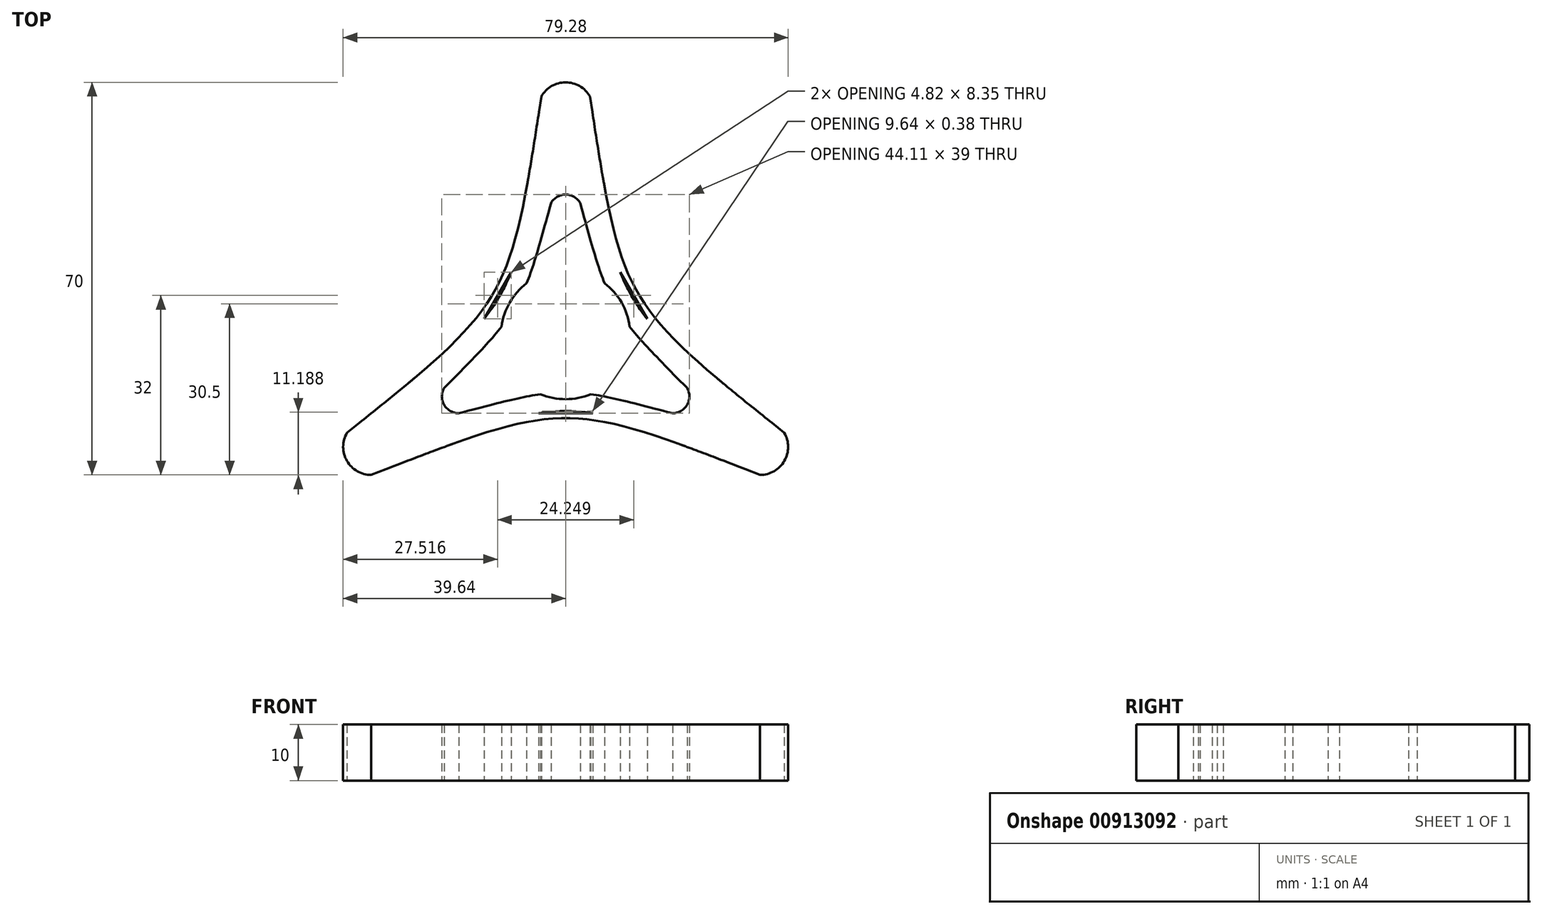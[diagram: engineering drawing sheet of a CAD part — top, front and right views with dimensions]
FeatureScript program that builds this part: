
annotation { "Feature Type Name" : "Feature", "Feature Type Description" : "" }
export const myFeature = defineFeature(function(context is Context, id is Id, definition is map)
    precondition{}
    {
        {
            var Q0;
            Q0=qCreatedBy(makeId("Top.planeOp"),FACE);
            var sketch = newSketch(context, id + "F0", { "sketchPlane" : qUnion([Q0])});
            skCircle(sketch, "E0", {"center": v(0, 0) * mm, "radius": 11.5 * mm});
            skCircle(sketch, "E1", {"center": v(0, 0) * mm, "radius": 40 * mm});
            skCircle(sketch, "E2", {"center": v(0, 0) * mm, "radius": 28 * mm});
            skCircle(sketch, "E3", {"center": v(0, 0) * mm, "radius": 9 * mm});
            skCircle(sketch, "E4.cCircle", {"center": v(0, 0) * mm, "radius": 9 * mm, "construction": true});
            skLineSegment(sketch, "E4.0", {"start": v(0, -9) * mm, "end": v(-7.8, 4.5) * mm});
            skLineSegment(sketch, "E4.1", {"start": v(-7.8, 4.5) * mm, "end": v(7.8, 4.5) * mm});
            skLineSegment(sketch, "E4.2", {"start": v(7.8, 4.5) * mm, "end": v(0, -9) * mm});
            skCircle(sketch, "E5.cCircle", {"center": v(0, 0) * mm, "radius": 11.5 * mm, "construction": true});
            skLineSegment(sketch, "E5.0", {"start": v(0, -11.5) * mm, "end": v(-9.96, 5.75) * mm});
            skLineSegment(sketch, "E5.1", {"start": v(-9.96, 5.75) * mm, "end": v(9.96, 5.75) * mm});
            skLineSegment(sketch, "E5.2", {"start": v(9.96, 5.75) * mm, "end": v(0, -11.5) * mm});
            skCircle(sketch, "E6.cCircle", {"center": v(0, 0) * mm, "radius": 28 * mm, "construction": true});
            skLineSegment(sketch, "E6.0", {"start": v(2.6, 23.5) * mm, "end": v(21.65, -9.5) * mm});
            skLineSegment(sketch, "E6.1", {"start": v(19.05, -14) * mm, "end": v(-19.05, -14) * mm});
            skLineSegment(sketch, "E6.2", {"start": v(-21.65, -9.5) * mm, "end": v(-2.6, 23.5) * mm});
            skCircle(sketch, "E7.cCircle", {"center": v(0, 0) * mm, "radius": 40 * mm, "construction": true});
            skPoint(sketch, "E7.cCircle.perimeterSnap0", {"position": v(0, 4.5) * mm});
            skLineSegment(sketch, "E7.0", {"start": v(4.33, 32.5) * mm, "end": v(30.31, -12.5) * mm});
            skPoint(sketch, "E7.0.startSnap0", {"position": v(0, 4.5) * mm});
            skLineSegment(sketch, "E7.1", {"start": v(25.98, -20) * mm, "end": v(-25.98, -20) * mm});
            skLineSegment(sketch, "E7.2", {"start": v(-30.31, -12.5) * mm, "end": v(-4.33, 32.5) * mm});
            skPoint(sketch, "E8.visualSharp", {"position": v(0, 40) * mm});
            skArc(sketch, "E8.filletArc", {"start": v(4.33, 32.5) * mm, "mid": v(0, 35) * mm, "end": v(-4.33, 32.5) * mm});
            skPoint(sketch, "E9.visualSharp", {"position": v(0, 28) * mm});
            skArc(sketch, "E9.filletArc", {"start": v(2.6, 23.5) * mm, "mid": v(0, 25) * mm, "end": v(-2.6, 23.5) * mm});
            skPoint(sketch, "E10.visualSharp", {"position": v(34.64, -20) * mm});
            skArc(sketch, "E10.filletArc", {"start": v(25.98, -20) * mm, "mid": v(30.31, -17.5) * mm, "end": v(30.31, -12.5) * mm});
            skPoint(sketch, "E11.visualSharp", {"position": v(24.25, -14) * mm});
            skArc(sketch, "E11.filletArc", {"start": v(19.05, -14) * mm, "mid": v(21.65, -12.5) * mm, "end": v(21.65, -9.5) * mm});
            skPoint(sketch, "E12.visualSharp", {"position": v(-24.25, -14) * mm});
            skArc(sketch, "E12.filletArc", {"start": v(-21.65, -9.5) * mm, "mid": v(-21.65, -12.5) * mm, "end": v(-19.05, -14) * mm});
            skPoint(sketch, "E13.visualSharp", {"position": v(-34.64, -20) * mm});
            skArc(sketch, "E13.filletArc", {"start": v(-30.31, -12.5) * mm, "mid": v(-30.31, -17.5) * mm, "end": v(-25.98, -20) * mm});
            skFitSpline(sketch, "E14", {"points": [v(4.33, 32.5) * mm, v(30.31, -12.5) * mm], "startDerivative": vector(16.89, -80.25) * mm, "endDerivative": vector(61.05, -54.75) * mm});
            skFitSpline(sketch, "E15", {"points": [v(2.6, 23.5) * mm, v(21.65, -9.5) * mm], "startDerivative": vector(15.59, -57) * mm, "endDerivative": vector(41.57, -42) * mm});
            skFitSpline(sketch, "E16", {"points": [v(-2.6, 23.5) * mm, v(-21.65, -9.5) * mm], "startDerivative": vector(-15.59, -57) * mm, "endDerivative": vector(-41.57, -42) * mm});
            skFitSpline(sketch, "E17", {"points": [v(-4.33, 32.5) * mm, v(-30.31, -12.5) * mm], "startDerivative": vector(-16.89, -80.25) * mm, "endDerivative": vector(-61.05, -54.75) * mm});
            skFitSpline(sketch, "E18", {"points": [v(-19.05, -14) * mm, v(19.05, -14) * mm], "startDerivative": vector(57.16, 15) * mm, "endDerivative": vector(57.16, -15) * mm});
            skFitSpline(sketch, "E19", {"points": [v(-25.98, -20) * mm, v(25.98, -20) * mm], "startDerivative": vector(77.94, 25.5) * mm, "endDerivative": vector(77.94, -25.5) * mm});
            skCircle(sketch, "E20", {"center": v(0, 0) * mm, "radius": 50 * mm});
            skCircle(sketch, "E21.cCircle", {"center": v(0, 0) * mm, "radius": 50 * mm, "construction": true});
            skLineSegment(sketch, "E21.0", {"start": v(4.33, 42.5) * mm, "end": v(38.97, -17.5) * mm});
            skLineSegment(sketch, "E21.1", {"start": v(34.64, -25) * mm, "end": v(-34.64, -25) * mm});
            skLineSegment(sketch, "E21.2", {"start": v(-38.97, -17.5) * mm, "end": v(-4.33, 42.5) * mm});
            skPoint(sketch, "E22.visualSharp", {"position": v(0, 50) * mm});
            skArc(sketch, "E22.filletArc", {"start": v(4.33, 42.5) * mm, "mid": v(0, 45) * mm, "end": v(-4.33, 42.5) * mm});
            skPoint(sketch, "E23.visualSharp", {"position": v(-43.3, -25) * mm});
            skArc(sketch, "E23.filletArc", {"start": v(-38.97, -17.5) * mm, "mid": v(-38.97, -22.5) * mm, "end": v(-34.64, -25) * mm});
            skPoint(sketch, "E24.visualSharp", {"position": v(43.3, -25) * mm});
            skArc(sketch, "E24.filletArc", {"start": v(34.64, -25) * mm, "mid": v(38.97, -22.5) * mm, "end": v(38.97, -17.5) * mm});
            skFitSpline(sketch, "E25", {"points": [v(4.33, 42.5) * mm, v(38.97, -17.5) * mm], "startDerivative": vector(16.89, -110.25) * mm, "endDerivative": vector(87.04, -69.75) * mm});
            skFitSpline(sketch, "E26", {"points": [v(-4.33, 42.5) * mm, v(-38.97, -17.5) * mm], "startDerivative": vector(-16.89, -110.25) * mm, "endDerivative": vector(-87.04, -69.75) * mm});
            skFitSpline(sketch, "E27", {"points": [v(-34.64, -25) * mm, v(34.64, -25) * mm], "startDerivative": vector(103.92, 40.5) * mm, "endDerivative": vector(103.92, -40.5) * mm});
            skSolve(sketch);
        }
        {
            var Q0;
            {var subQ5=sQuery(id+"F0.wireOp",EDGE,"E8.filletArc");Q0=makeQuery(id+"F0.imprint","IMPRINT",FACE,{"disambiguationData":[TD([[makeQuery(id+"F0.imprint","IMPRINT",EDGE,{"derivedFrom":subQ5}),1.0]])]});}
            var Q1;
            {var subQ0=sQuery(id+"F0.wireOp",EDGE,"E9.filletArc");Q1=makeQuery(id+"F0.imprint","IMPRINT",FACE,{"disambiguationData":[TD([[makeQuery(id+"F0.imprint","IMPRINT",EDGE,{"derivedFrom":subQ0}),-1.0]])]});}
            var Q2;
            {var subQ1=sQuery(id+"F0.wireOp",EDGE,"E6.0");var subQ3=sQuery(id+"F0.wireOp",EDGE,"E14");var subQ4=makeQuery(id+"F0.imprint","INTERSECT",VERTEX,{"disambiguationData":[OD(0.0)],"derivedFrom":[subQ1,subQ3]});Q2=makeQuery(id+"F0.imprint","IMPRINT",FACE,{"disambiguationData":[TD([[makeQuery(id+"F0.imprint","IMPRINT",EDGE,{"disambiguationData":[TD([[subQ4,-1.0]])],"derivedFrom":subQ3}),-1.0]])]});}
            var Q3;
            {var subQ5=sQuery(id+"F0.wireOp",EDGE,"E10.filletArc");Q3=makeQuery(id+"F0.imprint","IMPRINT",FACE,{"disambiguationData":[TD([[makeQuery(id+"F0.imprint","IMPRINT",EDGE,{"derivedFrom":subQ5}),1.0]])]});}
            var Q4;
            {var subQ0=sQuery(id+"F0.wireOp",EDGE,"E11.filletArc");Q4=makeQuery(id+"F0.imprint","IMPRINT",FACE,{"disambiguationData":[TD([[makeQuery(id+"F0.imprint","IMPRINT",EDGE,{"derivedFrom":subQ0}),-1.0]])]});}
            var Q5;
            {var subQ1=sQuery(id+"F0.wireOp",EDGE,"E6.1");var subQ3=sQuery(id+"F0.wireOp",EDGE,"E19");var subQ6=makeQuery(id+"F0.imprint","INTERSECT",VERTEX,{"disambiguationData":[OD(0.0)],"derivedFrom":[subQ1,subQ3]});Q5=makeQuery(id+"F0.imprint","IMPRINT",FACE,{"disambiguationData":[TD([[makeQuery(id+"F0.imprint","IMPRINT",EDGE,{"disambiguationData":[TD([[subQ6,1.0]])],"derivedFrom":subQ3}),1.0]])]});}
            var Q6;
            {var subQ0=sQuery(id+"F0.wireOp",EDGE,"E12.filletArc");Q6=makeQuery(id+"F0.imprint","IMPRINT",FACE,{"disambiguationData":[TD([[makeQuery(id+"F0.imprint","IMPRINT",EDGE,{"derivedFrom":subQ0}),-1.0]])]});}
            var Q7;
            {var subQ5=sQuery(id+"F0.wireOp",EDGE,"E13.filletArc");Q7=makeQuery(id+"F0.imprint","IMPRINT",FACE,{"disambiguationData":[TD([[makeQuery(id+"F0.imprint","IMPRINT",EDGE,{"derivedFrom":subQ5}),1.0]])]});}
            var Q8;
            {var subQ1=sQuery(id+"F0.wireOp",EDGE,"E6.2");var subQ3=sQuery(id+"F0.wireOp",EDGE,"E17");var subQ5=makeQuery(id+"F0.imprint","INTERSECT",VERTEX,{"disambiguationData":[OD(0.0)],"derivedFrom":[subQ1,subQ3]});Q8=makeQuery(id+"F0.imprint","IMPRINT",FACE,{"disambiguationData":[TD([[makeQuery(id+"F0.imprint","IMPRINT",EDGE,{"disambiguationData":[TD([[subQ5,1.0]])],"derivedFrom":subQ3}),1.0]])]});}
            extrude(context, id + "F1", {"entities" : qUnion([Q0, Q1, Q2, Q3, Q4, Q5, Q6, Q7, Q8]), "depth" : 10 * mm, "offsetDistance" : 25 * mm});
        }
        {
            var Q0;
            {var subQ5=sQuery(id+"F0.wireOp",EDGE,"E8.filletArc");Q0=makeQuery(id+"F0.imprint","IMPRINT",FACE,{"disambiguationData":[TD([[makeQuery(id+"F0.imprint","IMPRINT",EDGE,{"derivedFrom":subQ5}),1.0]])]});}
            var Q1;
            {var subQ0=sQuery(id+"F0.wireOp",EDGE,"E9.filletArc");Q1=makeQuery(id+"F0.imprint","IMPRINT",FACE,{"disambiguationData":[TD([[makeQuery(id+"F0.imprint","IMPRINT",EDGE,{"derivedFrom":subQ0}),-1.0]])]});}
            var Q2;
            {var subQ1=sQuery(id+"F0.wireOp",EDGE,"E6.2");var subQ3=sQuery(id+"F0.wireOp",EDGE,"E17");var subQ5=makeQuery(id+"F0.imprint","INTERSECT",VERTEX,{"disambiguationData":[OD(0.0)],"derivedFrom":[subQ1,subQ3]});Q2=makeQuery(id+"F0.imprint","IMPRINT",FACE,{"disambiguationData":[TD([[makeQuery(id+"F0.imprint","IMPRINT",EDGE,{"disambiguationData":[TD([[subQ5,1.0]])],"derivedFrom":subQ3}),1.0]])]});}
            var Q3;
            {var subQ1=sQuery(id+"F0.wireOp",EDGE,"E6.0");var subQ3=sQuery(id+"F0.wireOp",EDGE,"E14");var subQ4=makeQuery(id+"F0.imprint","INTERSECT",VERTEX,{"disambiguationData":[OD(0.0)],"derivedFrom":[subQ1,subQ3]});Q3=makeQuery(id+"F0.imprint","IMPRINT",FACE,{"disambiguationData":[TD([[makeQuery(id+"F0.imprint","IMPRINT",EDGE,{"disambiguationData":[TD([[subQ4,-1.0]])],"derivedFrom":subQ3}),-1.0]])]});}
            var Q4;
            {var subQ0=sQuery(id+"F0.wireOp",EDGE,"E11.filletArc");Q4=makeQuery(id+"F0.imprint","IMPRINT",FACE,{"disambiguationData":[TD([[makeQuery(id+"F0.imprint","IMPRINT",EDGE,{"derivedFrom":subQ0}),-1.0]])]});}
            var Q5;
            {var subQ5=sQuery(id+"F0.wireOp",EDGE,"E10.filletArc");Q5=makeQuery(id+"F0.imprint","IMPRINT",FACE,{"disambiguationData":[TD([[makeQuery(id+"F0.imprint","IMPRINT",EDGE,{"derivedFrom":subQ5}),1.0]])]});}
            var Q6;
            {var subQ1=sQuery(id+"F0.wireOp",EDGE,"E6.1");var subQ3=sQuery(id+"F0.wireOp",EDGE,"E19");var subQ6=makeQuery(id+"F0.imprint","INTERSECT",VERTEX,{"disambiguationData":[OD(0.0)],"derivedFrom":[subQ1,subQ3]});Q6=makeQuery(id+"F0.imprint","IMPRINT",FACE,{"disambiguationData":[TD([[makeQuery(id+"F0.imprint","IMPRINT",EDGE,{"disambiguationData":[TD([[subQ6,1.0]])],"derivedFrom":subQ3}),1.0]])]});}
            var Q7;
            {var subQ0=sQuery(id+"F0.wireOp",EDGE,"E12.filletArc");Q7=makeQuery(id+"F0.imprint","IMPRINT",FACE,{"disambiguationData":[TD([[makeQuery(id+"F0.imprint","IMPRINT",EDGE,{"derivedFrom":subQ0}),-1.0]])]});}
            var Q8;
            {var subQ5=sQuery(id+"F0.wireOp",EDGE,"E13.filletArc");Q8=makeQuery(id+"F0.imprint","IMPRINT",FACE,{"disambiguationData":[TD([[makeQuery(id+"F0.imprint","IMPRINT",EDGE,{"derivedFrom":subQ5}),1.0]])]});}
            extrude(context, id + "F2", {"entities" : qUnion([Q0, Q1, Q2, Q3, Q4, Q5, Q6, Q7, Q8]), "operationType" : NewBodyOperationType.ADD, "depth" : 10 * mm, "offsetDistance" : 25 * mm});
        }
        {
            var Q0;
            {var subQ5=sQuery(id+"F0.wireOp",EDGE,"E10.filletArc");Q0=makeQuery(id+"F0.imprint","IMPRINT",FACE,{"disambiguationData":[TD([[makeQuery(id+"F0.imprint","IMPRINT",EDGE,{"derivedFrom":subQ5}),1.0]])]});}
            var Q1;
            {var subQ0=sQuery(id+"F0.wireOp",EDGE,"E11.filletArc");Q1=makeQuery(id+"F0.imprint","IMPRINT",FACE,{"disambiguationData":[TD([[makeQuery(id+"F0.imprint","IMPRINT",EDGE,{"derivedFrom":subQ0}),-1.0]])]});}
            var Q2;
            {var subQ5=sQuery(id+"F0.wireOp",EDGE,"E8.filletArc");Q2=makeQuery(id+"F0.imprint","IMPRINT",FACE,{"disambiguationData":[TD([[makeQuery(id+"F0.imprint","IMPRINT",EDGE,{"derivedFrom":subQ5}),1.0]])]});}
            var Q3;
            {var subQ5=sQuery(id+"F0.wireOp",EDGE,"E13.filletArc");Q3=makeQuery(id+"F0.imprint","IMPRINT",FACE,{"disambiguationData":[TD([[makeQuery(id+"F0.imprint","IMPRINT",EDGE,{"derivedFrom":subQ5}),1.0]])]});}
            var Q4;
            {var subQ0=sQuery(id+"F0.wireOp",EDGE,"E12.filletArc");Q4=makeQuery(id+"F0.imprint","IMPRINT",FACE,{"disambiguationData":[TD([[makeQuery(id+"F0.imprint","IMPRINT",EDGE,{"derivedFrom":subQ0}),-1.0]])]});}
            var Q5;
            {var subQ0=sQuery(id+"F0.wireOp",EDGE,"E9.filletArc");Q5=makeQuery(id+"F0.imprint","IMPRINT",FACE,{"disambiguationData":[TD([[makeQuery(id+"F0.imprint","IMPRINT",EDGE,{"derivedFrom":subQ0}),-1.0]])]});}
            var Q6;
            {var subQ1=sQuery(id+"F0.wireOp",EDGE,"E6.0");var subQ3=sQuery(id+"F0.wireOp",EDGE,"E14");var subQ4=makeQuery(id+"F0.imprint","INTERSECT",VERTEX,{"disambiguationData":[OD(0.0)],"derivedFrom":[subQ1,subQ3]});Q6=makeQuery(id+"F0.imprint","IMPRINT",FACE,{"disambiguationData":[TD([[makeQuery(id+"F0.imprint","IMPRINT",EDGE,{"disambiguationData":[TD([[subQ4,-1.0]])],"derivedFrom":subQ3}),-1.0]])]});}
            var Q7;
            {var subQ1=sQuery(id+"F0.wireOp",EDGE,"E6.2");var subQ3=sQuery(id+"F0.wireOp",EDGE,"E17");var subQ5=makeQuery(id+"F0.imprint","INTERSECT",VERTEX,{"disambiguationData":[OD(0.0)],"derivedFrom":[subQ1,subQ3]});Q7=makeQuery(id+"F0.imprint","IMPRINT",FACE,{"disambiguationData":[TD([[makeQuery(id+"F0.imprint","IMPRINT",EDGE,{"disambiguationData":[TD([[subQ5,1.0]])],"derivedFrom":subQ3}),1.0]])]});}
            var Q8;
            {var subQ1=sQuery(id+"F0.wireOp",EDGE,"E6.1");var subQ3=sQuery(id+"F0.wireOp",EDGE,"E19");var subQ6=makeQuery(id+"F0.imprint","INTERSECT",VERTEX,{"disambiguationData":[OD(0.0)],"derivedFrom":[subQ1,subQ3]});Q8=makeQuery(id+"F0.imprint","IMPRINT",FACE,{"disambiguationData":[TD([[makeQuery(id+"F0.imprint","IMPRINT",EDGE,{"disambiguationData":[TD([[subQ6,1.0]])],"derivedFrom":subQ3}),1.0]])]});}
            extrude(context, id + "F3", {"entities" : qUnion([Q0, Q1, Q2, Q3, Q4, Q5, Q6, Q7, Q8]), "operationType" : NewBodyOperationType.ADD, "depth" : 10 * mm, "offsetDistance" : 25 * mm});
        }
        {
            var Q0;
            {var subQ0=sQuery(id+"F0.wireOp",EDGE,"E8.filletArc");Q0=makeQuery(id+"F0.imprint","IMPRINT",FACE,{"disambiguationData":[TD([[makeQuery(id+"F0.imprint","IMPRINT",EDGE,{"derivedFrom":subQ0}),-1.0]])]});}
            var Q1;
            {var subQ5=sQuery(id+"F0.wireOp",EDGE,"E22.filletArc");Q1=makeQuery(id+"F0.imprint","IMPRINT",FACE,{"disambiguationData":[TD([[makeQuery(id+"F0.imprint","IMPRINT",EDGE,{"derivedFrom":subQ5}),1.0]])]});}
            var Q2;
            {var subQ0=sQuery(id+"F0.wireOp",EDGE,"E9.filletArc");Q2=makeQuery(id+"F0.imprint","IMPRINT",FACE,{"disambiguationData":[TD([[makeQuery(id+"F0.imprint","IMPRINT",EDGE,{"derivedFrom":subQ0}),-1.0]])]});}
            var Q3;
            {var subQ5=sQuery(id+"F0.wireOp",EDGE,"E8.filletArc");Q3=makeQuery(id+"F0.imprint","IMPRINT",FACE,{"disambiguationData":[TD([[makeQuery(id+"F0.imprint","IMPRINT",EDGE,{"derivedFrom":subQ5}),1.0]])]});}
            var Q4;
            {var subQ0=sQuery(id+"F0.wireOp",EDGE,"E25");var subQ1=sQuery(id+"F0.wireOp",EDGE,"E2");var subQ2=makeQuery(id+"F0.imprint","INTERSECT",VERTEX,{"disambiguationData":[OD(0.0)],"derivedFrom":[subQ1,subQ0]});Q4=makeQuery(id+"F0.imprint","IMPRINT",FACE,{"disambiguationData":[TD([[makeQuery(id+"F0.imprint","IMPRINT",EDGE,{"disambiguationData":[TD([[subQ2,-1.0]])],"derivedFrom":subQ1}),-1.0]])]});}
            var Q5;
            {var subQ0=sQuery(id+"F0.wireOp",EDGE,"E17");var subQ1=sQuery(id+"F0.wireOp",EDGE,"E2");var subQ2=makeQuery(id+"F0.imprint","INTERSECT",VERTEX,{"disambiguationData":[OD(0.0)],"derivedFrom":[subQ1,subQ0]});Q5=makeQuery(id+"F0.imprint","IMPRINT",FACE,{"disambiguationData":[TD([[makeQuery(id+"F0.imprint","IMPRINT",EDGE,{"disambiguationData":[TD([[subQ2,-1.0]])],"derivedFrom":subQ1}),-1.0]])]});}
            var Q6;
            {var subQ0=sQuery(id+"F0.wireOp",EDGE,"E17");var subQ1=sQuery(id+"F0.wireOp",EDGE,"E2");var subQ2=makeQuery(id+"F0.imprint","INTERSECT",VERTEX,{"disambiguationData":[OD(0.0)],"derivedFrom":[subQ1,subQ0]});Q6=makeQuery(id+"F0.imprint","IMPRINT",FACE,{"disambiguationData":[TD([[makeQuery(id+"F0.imprint","IMPRINT",EDGE,{"disambiguationData":[TD([[subQ2,-1.0]])],"derivedFrom":subQ1}),1.0]])]});}
            var Q7;
            {var subQ1=sQuery(id+"F0.wireOp",EDGE,"E2");var subQ7=sQuery(id+"F0.wireOp",EDGE,"E25");var subQ9=makeQuery(id+"F0.imprint","INTERSECT",VERTEX,{"disambiguationData":[OD(0.0)],"derivedFrom":[subQ1,subQ7]});Q7=makeQuery(id+"F0.imprint","IMPRINT",FACE,{"disambiguationData":[TD([[makeQuery(id+"F0.imprint","IMPRINT",EDGE,{"disambiguationData":[TD([[subQ9,-1.0]])],"derivedFrom":subQ1}),1.0]])]});}
            var Q8;
            {var subQ1=sQuery(id+"F0.wireOp",EDGE,"E6.0");var subQ3=sQuery(id+"F0.wireOp",EDGE,"E14");var subQ8=makeQuery(id+"F0.imprint","INTERSECT",VERTEX,{"disambiguationData":[OD(0.0)],"derivedFrom":[subQ1,subQ3]});Q8=makeQuery(id+"F0.imprint","IMPRINT",FACE,{"disambiguationData":[TD([[makeQuery(id+"F0.imprint","IMPRINT",EDGE,{"disambiguationData":[TD([[subQ8,-1.0]])],"derivedFrom":subQ3}),-1.0]])]});}
            var Q9;
            {var subQ0=sQuery(id+"F0.wireOp",EDGE,"E14");var subQ1=sQuery(id+"F0.wireOp",EDGE,"E6.0");var subQ2=makeQuery(id+"F0.imprint","INTERSECT",VERTEX,{"disambiguationData":[OD(0.0)],"derivedFrom":[subQ1,subQ0]});Q9=makeQuery(id+"F0.imprint","IMPRINT",FACE,{"disambiguationData":[TD([[makeQuery(id+"F0.imprint","IMPRINT",EDGE,{"disambiguationData":[TD([[subQ2,-1.0]])],"derivedFrom":subQ1}),-1.0]])]});}
            var Q10;
            {var subQ0=sQuery(id+"F0.wireOp",EDGE,"E11.filletArc");Q10=makeQuery(id+"F0.imprint","IMPRINT",FACE,{"disambiguationData":[TD([[makeQuery(id+"F0.imprint","IMPRINT",EDGE,{"derivedFrom":subQ0}),-1.0]])]});}
            var Q11;
            {var subQ0=sQuery(id+"F0.wireOp",EDGE,"E14");var subQ1=sQuery(id+"F0.wireOp",EDGE,"E2");var subQ2=makeQuery(id+"F0.imprint","INTERSECT",VERTEX,{"disambiguationData":[OD(1.0)],"derivedFrom":[subQ1,subQ0]});Q11=makeQuery(id+"F0.imprint","IMPRINT",FACE,{"disambiguationData":[TD([[makeQuery(id+"F0.imprint","IMPRINT",EDGE,{"disambiguationData":[TD([[subQ2,-1.0]])],"derivedFrom":subQ1}),-1.0]])]});}
            var Q12;
            {var subQ0=sQuery(id+"F0.wireOp",EDGE,"E10.filletArc");Q12=makeQuery(id+"F0.imprint","IMPRINT",FACE,{"disambiguationData":[TD([[makeQuery(id+"F0.imprint","IMPRINT",EDGE,{"derivedFrom":subQ0}),-1.0]])]});}
            var Q13;
            {var subQ5=sQuery(id+"F0.wireOp",EDGE,"E10.filletArc");Q13=makeQuery(id+"F0.imprint","IMPRINT",FACE,{"disambiguationData":[TD([[makeQuery(id+"F0.imprint","IMPRINT",EDGE,{"derivedFrom":subQ5}),1.0]])]});}
            var Q14;
            {var subQ5=sQuery(id+"F0.wireOp",EDGE,"E24.filletArc");Q14=makeQuery(id+"F0.imprint","IMPRINT",FACE,{"disambiguationData":[TD([[makeQuery(id+"F0.imprint","IMPRINT",EDGE,{"derivedFrom":subQ5}),1.0]])]});}
            var Q15;
            {var subQ0=sQuery(id+"F0.wireOp",EDGE,"E27");var subQ1=sQuery(id+"F0.wireOp",EDGE,"E2");var subQ2=makeQuery(id+"F0.imprint","INTERSECT",VERTEX,{"disambiguationData":[OD(1.0)],"derivedFrom":[subQ1,subQ0]});Q15=makeQuery(id+"F0.imprint","IMPRINT",FACE,{"disambiguationData":[TD([[makeQuery(id+"F0.imprint","IMPRINT",EDGE,{"disambiguationData":[TD([[subQ2,-1.0]])],"derivedFrom":subQ1}),-1.0]])]});}
            var Q16;
            {var subQ0=sQuery(id+"F0.wireOp",EDGE,"E19");var subQ1=sQuery(id+"F0.wireOp",EDGE,"E2");var subQ2=makeQuery(id+"F0.imprint","INTERSECT",VERTEX,{"disambiguationData":[OD(0.0)],"derivedFrom":[subQ1,subQ0]});Q16=makeQuery(id+"F0.imprint","IMPRINT",FACE,{"disambiguationData":[TD([[makeQuery(id+"F0.imprint","IMPRINT",EDGE,{"disambiguationData":[TD([[subQ2,-1.0]])],"derivedFrom":subQ1}),1.0]])]});}
            var Q17;
            {var subQ1=sQuery(id+"F0.wireOp",EDGE,"E6.1");var subQ3=sQuery(id+"F0.wireOp",EDGE,"E19");var subQ4=makeQuery(id+"F0.imprint","INTERSECT",VERTEX,{"disambiguationData":[OD(0.0)],"derivedFrom":[subQ1,subQ3]});Q17=makeQuery(id+"F0.imprint","IMPRINT",FACE,{"disambiguationData":[TD([[makeQuery(id+"F0.imprint","IMPRINT",EDGE,{"disambiguationData":[TD([[subQ4,1.0]])],"derivedFrom":subQ3}),1.0]])]});}
            var Q18;
            {var subQ0=sQuery(id+"F0.wireOp",EDGE,"E19");var subQ1=sQuery(id+"F0.wireOp",EDGE,"E6.1");var subQ2=makeQuery(id+"F0.imprint","INTERSECT",VERTEX,{"disambiguationData":[OD(0.0)],"derivedFrom":[subQ1,subQ0]});Q18=makeQuery(id+"F0.imprint","IMPRINT",FACE,{"disambiguationData":[TD([[makeQuery(id+"F0.imprint","IMPRINT",EDGE,{"disambiguationData":[TD([[subQ2,-1.0]])],"derivedFrom":subQ1}),-1.0]])]});}
            var Q19;
            {var subQ5=sQuery(id+"F0.wireOp",EDGE,"E23.filletArc");Q19=makeQuery(id+"F0.imprint","IMPRINT",FACE,{"disambiguationData":[TD([[makeQuery(id+"F0.imprint","IMPRINT",EDGE,{"derivedFrom":subQ5}),1.0]])]});}
            var Q20;
            {var subQ0=sQuery(id+"F0.wireOp",EDGE,"E13.filletArc");Q20=makeQuery(id+"F0.imprint","IMPRINT",FACE,{"disambiguationData":[TD([[makeQuery(id+"F0.imprint","IMPRINT",EDGE,{"derivedFrom":subQ0}),-1.0]])]});}
            var Q21;
            {var subQ5=sQuery(id+"F0.wireOp",EDGE,"E13.filletArc");Q21=makeQuery(id+"F0.imprint","IMPRINT",FACE,{"disambiguationData":[TD([[makeQuery(id+"F0.imprint","IMPRINT",EDGE,{"derivedFrom":subQ5}),1.0]])]});}
            var Q22;
            {var subQ0=sQuery(id+"F0.wireOp",EDGE,"E19");var subQ1=sQuery(id+"F0.wireOp",EDGE,"E2");var subQ2=makeQuery(id+"F0.imprint","INTERSECT",VERTEX,{"disambiguationData":[OD(0.0)],"derivedFrom":[subQ1,subQ0]});Q22=makeQuery(id+"F0.imprint","IMPRINT",FACE,{"disambiguationData":[TD([[makeQuery(id+"F0.imprint","IMPRINT",EDGE,{"disambiguationData":[TD([[subQ2,-1.0]])],"derivedFrom":subQ1}),-1.0]])]});}
            var Q23;
            {var subQ0=sQuery(id+"F0.wireOp",EDGE,"E26");var subQ1=sQuery(id+"F0.wireOp",EDGE,"E2");var subQ2=makeQuery(id+"F0.imprint","INTERSECT",VERTEX,{"disambiguationData":[OD(1.0)],"derivedFrom":[subQ1,subQ0]});Q23=makeQuery(id+"F0.imprint","IMPRINT",FACE,{"disambiguationData":[TD([[makeQuery(id+"F0.imprint","IMPRINT",EDGE,{"disambiguationData":[TD([[subQ2,-1.0]])],"derivedFrom":subQ1}),-1.0]])]});}
            var Q24;
            {var subQ0=sQuery(id+"F0.wireOp",EDGE,"E12.filletArc");Q24=makeQuery(id+"F0.imprint","IMPRINT",FACE,{"disambiguationData":[TD([[makeQuery(id+"F0.imprint","IMPRINT",EDGE,{"derivedFrom":subQ0}),-1.0]])]});}
            var Q25;
            {var subQ1=sQuery(id+"F0.wireOp",EDGE,"E6.2");var subQ3=sQuery(id+"F0.wireOp",EDGE,"E17");var subQ10=makeQuery(id+"F0.imprint","INTERSECT",VERTEX,{"disambiguationData":[OD(0.0)],"derivedFrom":[subQ1,subQ3]});Q25=makeQuery(id+"F0.imprint","IMPRINT",FACE,{"disambiguationData":[TD([[makeQuery(id+"F0.imprint","IMPRINT",EDGE,{"disambiguationData":[TD([[subQ10,1.0]])],"derivedFrom":subQ3}),1.0]])]});}
            var Q26;
            {var subQ0=sQuery(id+"F0.wireOp",EDGE,"E17");var subQ1=sQuery(id+"F0.wireOp",EDGE,"E6.2");var subQ2=makeQuery(id+"F0.imprint","INTERSECT",VERTEX,{"disambiguationData":[OD(0.0)],"derivedFrom":[subQ1,subQ0]});Q26=makeQuery(id+"F0.imprint","IMPRINT",FACE,{"disambiguationData":[TD([[makeQuery(id+"F0.imprint","IMPRINT",EDGE,{"disambiguationData":[TD([[subQ2,-1.0]])],"derivedFrom":subQ1}),-1.0]])]});}
            extrude(context, id + "F4", {"entities" : qUnion([Q0, Q1, Q2, Q3, Q4, Q5, Q6, Q7, Q8, Q9, Q10, Q11, Q12, Q13, Q14, Q15, Q16, Q17, Q18, Q19, Q20, Q21, Q22, Q23, Q24, Q25, Q26]), "operationType" : NewBodyOperationType.ADD, "depth" : 10 * mm, "offsetDistance" : 25 * mm});
        }
    });
